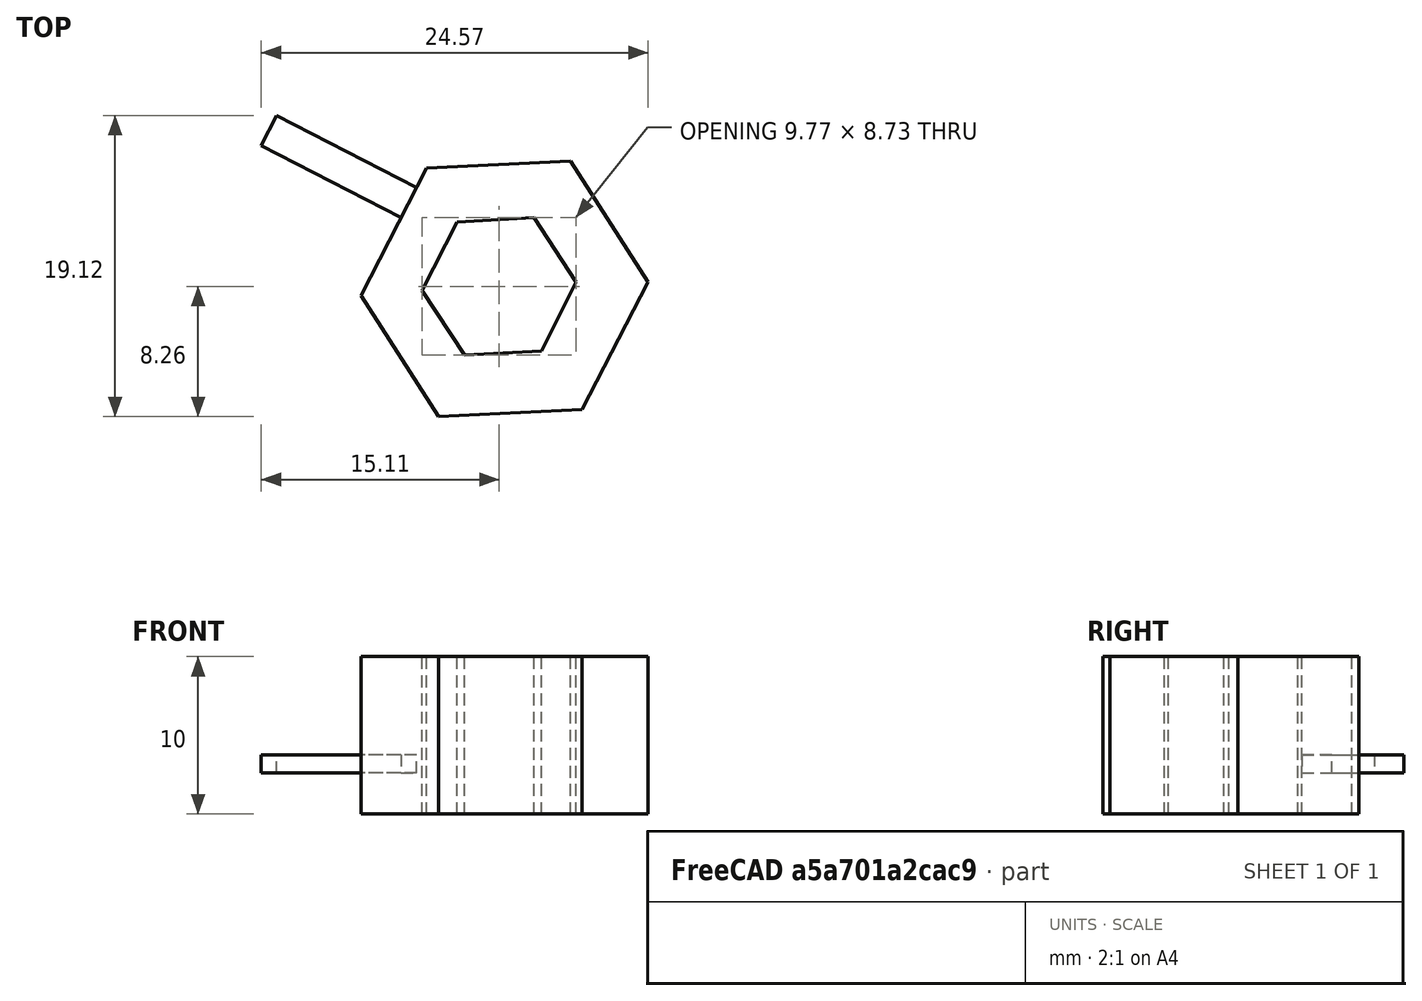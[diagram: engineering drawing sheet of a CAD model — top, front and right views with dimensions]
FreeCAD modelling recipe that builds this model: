
FCSTD DOCUMENT  (FreeCAD 0.18R16131 (Git))
Label: Temperature Simulation 1
License: All rights reserved
LicenseURL: http://en.wikipedia.org/wiki/All_rights_reserved
objects: Sketcher::SketchObject×2, PartDesign::Pad×2, Fem::FemMeshObjectPython×2, PartDesign::Body×1, App::MaterialObjectPython×1, Fem::ConstraintInitialTemperature×1, Fem::ConstraintTemperature×1, Fem::FemSolverObjectPython×1, Fem::FemResultObjectPython×1, Fem::FemAnalysis×1
note: 7 computed .brp shape members not serialized (recipe doc carries the construction recipe); baked Part::Feature solids carry a one-line shape summary decoded from their .brp

FEATURE [Sketcher::SketchObject] Sketch
  MapMode = 5
  Support = -> [XY_Plane]
  sketch-geometry (14):
    g0: LineSegment StartX=4.88634 StartY=0.271548 StartZ=0 EndX=2.208 EndY=4.36746 EndZ=0
    g1: LineSegment StartX=2.208 StartY=4.36746 StartZ=0 EndX=-2.67834 EndY=4.09591 EndZ=0
    g2: LineSegment StartX=-2.67834 StartY=4.09591 StartZ=0 EndX=-4.88634 EndY=-0.271554 EndZ=0
    g3: LineSegment StartX=-4.88634 StartY=-0.271554 StartZ=0 EndX=-2.208 EndY=-4.36747 EndZ=0
    g4: LineSegment StartX=-2.208 StartY=-4.36747 StartZ=0 EndX=2.67834 EndY=-4.09592 EndZ=0
    g5: LineSegment StartX=2.67834 StartY=-4.09592 StartZ=0 EndX=4.88634 EndY=0.271548 EndZ=0
    g6: Circle [constr] CenterX=-4e-16 CenterY=-3e-06 CenterZ=0 NormalX=0 NormalY=0 NormalZ=1 AngleXU=0 Radius=4.89388
    g7: LineSegment StartX=-8.78087 StartY=-0.578961 StartZ=0 EndX=-3.84553 EndY=-8.25879 EndZ=0
    g8: LineSegment StartX=-3.84553 StartY=-8.25879 StartZ=0 EndX=5.27307 EndY=-7.82457 EndZ=0
    g9: LineSegment StartX=5.27307 StartY=-7.82457 StartZ=0 EndX=9.45632 EndY=0.289475 EndZ=0
    g10: LineSegment StartX=9.45632 StartY=0.289475 StartZ=0 EndX=4.52098 EndY=7.9693 EndZ=0
    g11: LineSegment StartX=4.52098 StartY=7.9693 StartZ=0 EndX=-4.59762 EndY=7.53508 EndZ=0
    g12: LineSegment StartX=-4.59762 StartY=7.53508 StartZ=0 EndX=-8.78087 EndY=-0.578961 EndZ=0
    g13: Circle [constr] CenterX=0.337726 CenterY=-0.144743 CenterZ=0 NormalX=0 NormalY=0 NormalZ=1 AngleXU=0 Radius=9.12893
  constraints (26):
    c: Coincident(g0,g1)
    c: Coincident(g1,g2)
    c: Coincident(g2,g3)
    c: Coincident(g3,g4)
    c: Coincident(g4,g5)
    c: Coincident(g5,g0)
    c: Equal(g0, g1-g5) x5
    c: PointOnObject(g0,g6)
    c: PointOnObject(g1,g6)
    c: PointOnObject(g2,g6)
    c: PointOnObject(g3,g6)
    c: PointOnObject(g4,g6)
    c: PointOnObject(g5,g6)
    c: Coincident(g7,g8)
    c: Coincident(g8,g9)
    c: Coincident(g9,g10)
    c: Coincident(g10,g11)
    c: Coincident(g11,g12)
    c: Coincident(g12,g7)
    c: Equal(g7, g8-g12) x5
    c: PointOnObject(g7,g13)
    c: PointOnObject(g8,g13)
    c: PointOnObject(g9,g13)
    c: PointOnObject(g10,g13)
    c: PointOnObject(g11,g13)
    c: PointOnObject(g12,g13)
FEATURE [PartDesign::Pad] Pad
  Length = 10
  Length2 = 100
  Profile = -> Sketch
  Type = 0
FEATURE [Sketcher::SketchObject] Sketch002
  MapMode = 5
  Placement = pos=(-6.70121,3.45486,0) rot=(-0.395799,0.649362,0.649362;3.89535rad)
  sketch-geometry (4):
    g0: LineSegment StartX=-3.17125 StartY=3.76481 StartZ=0 EndX=-1.03677 EndY=3.76481 EndZ=0
    g1: LineSegment StartX=-1.03677 StartY=3.76481 StartZ=0 EndX=-1.03677 EndY=2.60055 EndZ=0
    g2: LineSegment StartX=-1.03677 StartY=2.60055 StartZ=0 EndX=-3.17125 EndY=2.60055 EndZ=0
    g3: LineSegment StartX=-3.17125 StartY=2.60055 StartZ=0 EndX=-3.17125 EndY=3.76481 EndZ=0
  constraints (8):
    c: Coincident(g0,g1)
    c: Coincident(g1,g2)
    c: Coincident(g2,g3)
    c: Coincident(g3,g0)
    c: Horizontal(g0)
    c: Horizontal(g2)
    c: Vertical(g1)
    c: Vertical(g3)
FEATURE [PartDesign::Pad] Pad001
  BaseFeature = -> Pad
  Length = 10
  Length2 = 100
  Profile = -> Sketch002
  Type = 0
FEATURE [PartDesign::Body] Body
  Group = -> [Sketch,Pad,Sketch002,Pad001]
  Origin = -> Origin
  Tip = -> Pad001
FEATURE [App::MaterialObjectPython] SolidMaterial  # material (typed FeaturePython)
  Category = 0
  Material = Density=7900.000000000001 kg/m^3,Description=Standard steel material for CalculiX sample calculations,Father=Metal,Name=CalculiX-Steel,+5 more (map truncated)
  References = -> [Pad001]
FEATURE [Fem::ConstraintInitialTemperature] FemConstraintInitialTemperature
  NormalDirection = (0,0,1)
  initialTemperature = 300
FEATURE [Fem::ConstraintTemperature] FemConstraintTemperature
  CFlux = 0
  ConstraintType = 1
  NormalDirection = (-0.888828,0.458242,4e-16)
  Normals = (9) [(-0.888828,0.458242,3.6e-16),(-0.888828,0.458242,3.6e-16),(-0.888828,0.458242,3.6e-16),(-0.888828,0.458242,3.6e-16),(-0.888828,0.458242,3.6e-16),+4 more]
  Points = (9) [(-15.1144,8.95878,2.60055),(-14.6253,9.90737,2.60055),(-14.1363,10.856,2.60055),(-15.1144,8.95878,3.18268),(-14.6253,9.90737,3.18268),+4 more]
  References = -> [Pad001]
  Temperature = 1200
FEATURE [Fem::FemSolverObjectPython] CalculiXccxTools  # FEM object (typed FeaturePython)
  AnalysisType = 2
  BeamShellResultOutput3D = false
  EigenmodeHighLimit = 1000000
  EigenmodeLowLimit = 0
  EigenmodesCount = 10
  GeometricalNonlinearity = 0
  IterationsControlParameterCutb = 0.25,0.5,0.75,0.85,,,1.5,
  IterationsControlParameterIter = 4,8,9,200,10,400,,200,,
  IterationsControlParameterTimeUse = false
  IterationsThermoMechMaximum = 2000
  IterationsUserDefinedIncrementations = false
  IterationsUserDefinedTimeStepLength = false
  MaterialNonlinearity = 0
  MatrixSolverType = 0
  SplitInputWriter = false
  ThermoMechSteadyState = true
  TimeEnd = 1
  TimeInitialStep = 1
FEATURE [Fem::FemMeshObjectPython] FEMMeshGmsh  # FEM object (typed FeaturePython)
  Algorithm2D = 0
  Algorithm3D = 0
  CharacteristicLengthMax = 1
  CharacteristicLengthMin = 0
  CoherenceMesh = true
  ElementDimension = 0
  ElementOrder = 1
  GeometryTolerance = 1e-06
  GroupsOfNodes = false
  HighOrderOptimize = false
  OptimizeNetgen = false
  OptimizeStd = true
  Part = -> Pad001
  RecombineAll = false
FEATURE [Fem::FemMeshObjectPython] Result_mesh  # FEM object (typed FeaturePython)
FEATURE [Fem::FemResultObjectPython] CalculiX_thermomech_results  # FEM object (typed FeaturePython)
  DisplacementLengths = [0.387,0.357127,0.349365,0.317848,0.347316,0.338256,0.329426,0.324917,0.32798,0.331792,0.254872,0.247285,0.184451,0.248954,0.143258,0.0646447,0.233174,0.268913,0.237676,0.149003,0.215013,0.270159,0.125557,0.0892322,0.200859,0.239924,+15453 more]
  DisplacementVectors = (15479) [(-0.10884,-0.364138,-0.0729842),(-0.126739,-0.33204,0.0350158),(0.164523,-0.30566,-0.0394995),(0.146624,-0.273562,0.0685005),+15475 more]
  Eigenmode = 0
  EigenmodeFrequency = 0
  MaxShear = [1.41171e-10,1.98847e-10,8.78946e-11,1.7361e-10,3.39537e-10,7.57017e-11,6.13148e-10,7.9136e-10,6.3814e-10,8.14638e-10,9.68648e-11,1.13241e-10,6.16879e-11,4.04013e-11,2.16264e-10,6.91478e-11,7.11961e-11,4.38692e-11,1.92825e-10,1.35476e-10,+15459 more]
  Mesh = -> Result_mesh
  NodeNumbers = [1,2,3,4,5,6,7,8,9,10,11,12,13,14,15,16,17,18,19,20,21,22,23,24,25,26,27,28,29,30,31,32,33,34,35,36,37,38,39,40,41,42,43,44,45,46,47,48,49,50,51,52,53,54,55,56,57,58,59,60,61,62,63,64,65,66,67,68,69,+15410 more]
  PrincipalMax = [2.04496e-09,2.03151e-09,1.89556e-09,1.89499e-09,1.94586e-09,1.84719e-09,1.55242e-09,1.36326e-09,3.1791e-09,3.73306e-09,1.92346e-09,1.91129e-09,1.87486e-09,1.78108e-09,1.79693e-09,1.75474e-09,1.88727e-09,1.88583e-09,1.72323e-09,1.91369e-09,+15459 more]
  PrincipalMed = [1.80431e-09,1.75635e-09,1.82765e-09,1.81061e-09,1.69731e-09,1.77828e-09,1.48512e-09,1.23188e-09,2.12693e-09,2.18796e-09,1.73324e-09,1.76392e-09,1.76918e-09,1.75017e-09,1.70428e-09,1.73813e-09,1.8127e-09,1.83881e-09,1.622e-09,1.75119e-09,+15459 more]
  PrincipalMin = [1.76261e-09,1.63382e-09,1.71977e-09,1.54777e-09,1.26678e-09,1.69579e-09,3.26124e-10,-2.19462e-10,1.90282e-09,2.10379e-09,1.72973e-09,1.68481e-09,1.75148e-09,1.70028e-09,1.36441e-09,1.61645e-09,1.74488e-09,1.79809e-09,1.33758e-09,+15460 more]
  ResultType = Fem::FemResultMechanical
  Stats = [-0.501079,-0.0461041,0.250562,-0.434267,-0.0929744,0.199917,-0.0915415,-0.00718724,0.0834281,0.0393479,0.230486,0.637272,7.68171e-12,1.60651e-10,4.74808e-09,6.43765e-11,1.80997e-09,6.45655e-09,-2.58308e-10,1.72885e-09,2.65014e-09,+18 more]
  StressValues = [2.63976e-10,3.52766e-10,1.53544e-10,3.13662e-10,5.95092e-10,1.31295e-10,1.19407e-09,1.52129e-09,1.18029e-09,1.58886e-09,1.91999e-10,1.99087e-10,1.15548e-10,7.06182e-11,3.94448e-10,1.30784e-10,1.23361e-10,7.60488e-11,3.46315e-10,2.36203e-10,+15459 more]
  StressVectors = (15479) [(1.79034e-09,1.94886e-09,1.87268e-09),(1.85817e-09,1.79861e-09,1.7649e-09),(1.79717e-09,1.87349e-09,1.77232e-09),+15476 more]
  Time = 1
  UserDefined = [2.82342e-10,3.97694e-10,1.75789e-10,3.4722e-10,6.79074e-10,1.51403e-10,1.2263e-09,1.58272e-09,1.27628e-09,1.62928e-09,1.9373e-10,2.26482e-10,1.23376e-10,8.08027e-11,4.32528e-10,1.38296e-10,1.42392e-10,8.77384e-11,3.8565e-10,2.70953e-10,+15459 more]
FEATURE [Fem::FemAnalysis] Analysis
  Group = -> [SolidMaterial,FemConstraintInitialTemperature,FemConstraintTemperature,CalculiXccxTools,FEMMeshGmsh,CalculiX_thermomech_results]
